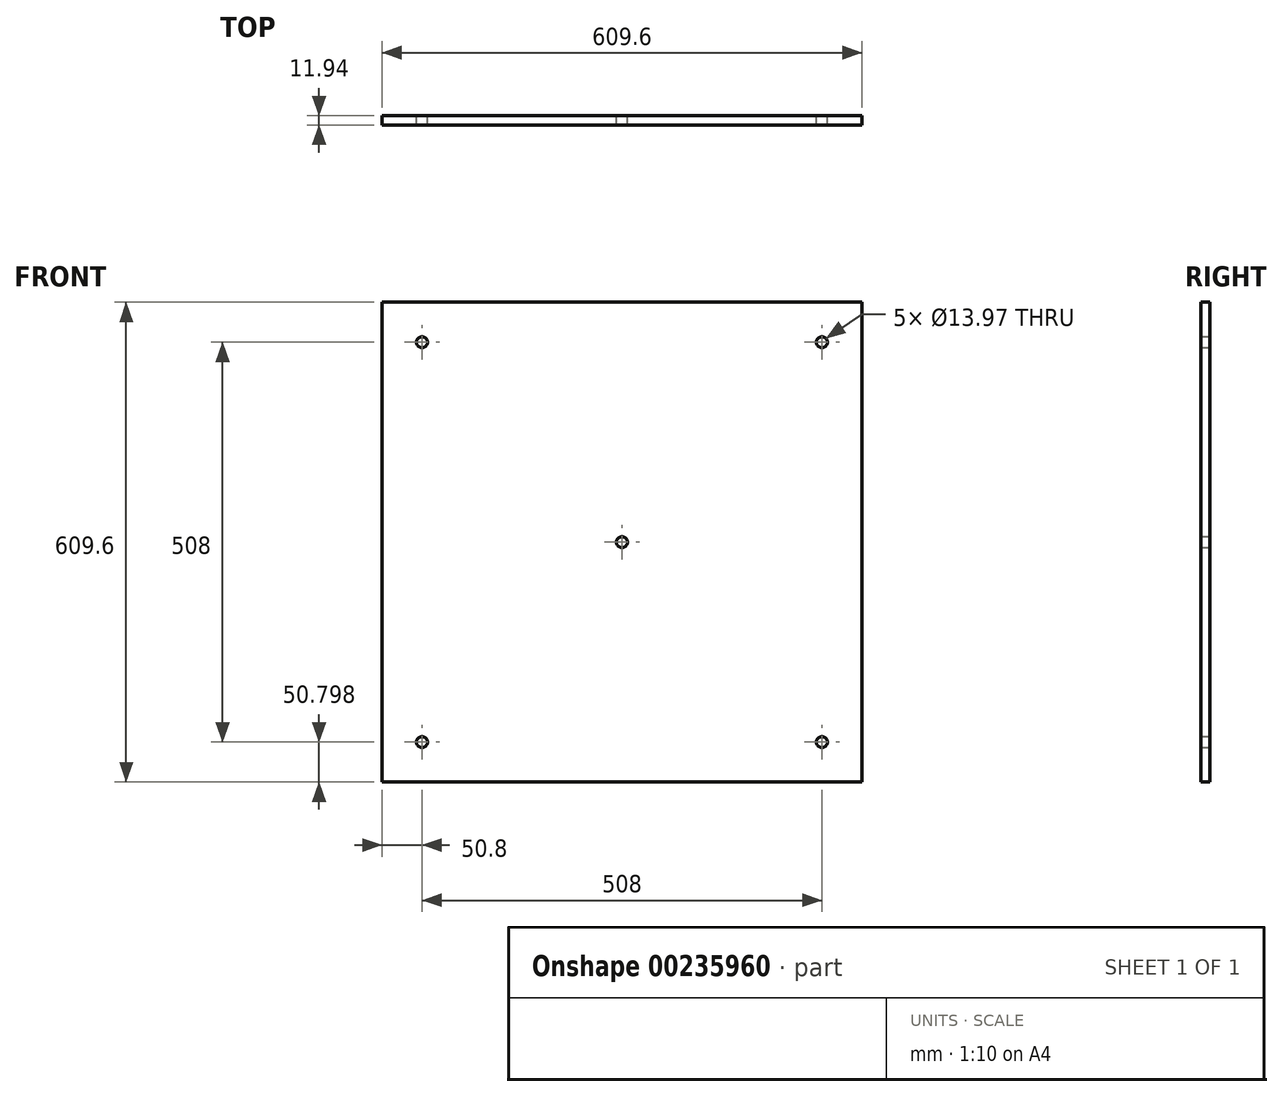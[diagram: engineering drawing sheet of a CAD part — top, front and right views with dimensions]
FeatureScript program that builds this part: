
annotation { "Feature Type Name" : "Feature", "Feature Type Description" : "" }
export const myFeature = defineFeature(function(context is Context, id is Id, definition is map)
    precondition{}
    {
        {
            var Q0;
            Q0=qCreatedBy(makeId("Front.planeOp"),FACE);
            var sketch = newSketch(context, id + "F0", { "sketchPlane" : qUnion([Q0])});
            skLineSegment(sketch, "E0.bottom", {"start": v(-264.46, 453.03) * mm, "end": v(345.14, 453.03) * mm});
            skLineSegment(sketch, "E0.top", {"start": v(-264.46, -156.57) * mm, "end": v(345.14, -156.57) * mm});
            skLineSegment(sketch, "E0.left", {"start": v(-264.46, 453.03) * mm, "end": v(-264.46, -156.57) * mm});
            skLineSegment(sketch, "E0.right", {"start": v(345.14, 453.03) * mm, "end": v(345.14, -156.57) * mm});
            skCircle(sketch, "E1", {"center": v(-213.66, 402.23) * mm, "radius": 6.99 * mm});
            skCircle(sketch, "E2", {"center": v(294.34, 402.23) * mm, "radius": 6.99 * mm});
            skCircle(sketch, "E3", {"center": v(-213.66, -105.77) * mm, "radius": 6.99 * mm});
            skCircle(sketch, "E4", {"center": v(294.34, -105.77) * mm, "radius": 6.99 * mm});
            skCircle(sketch, "E5", {"center": v(40.34, 148.23) * mm, "radius": 6.99 * mm});
            skSolve(sketch);
        }
        {
            var Q0;
            Q0=makeQuery(id+"F0.imprint","IMPRINT",FACE,{"disambiguationData":[TD([[makeQuery(id+"F0.imprint","IMPRINT",EDGE,{"derivedFrom":sQuery(id+"F0.wireOp",EDGE,"E0.bottom")}),-1.0]])]});
            extrude(context, id + "F1", {"entities" : qUnion([Q0]), "depth" : 11.94 * mm});
        }
    });
